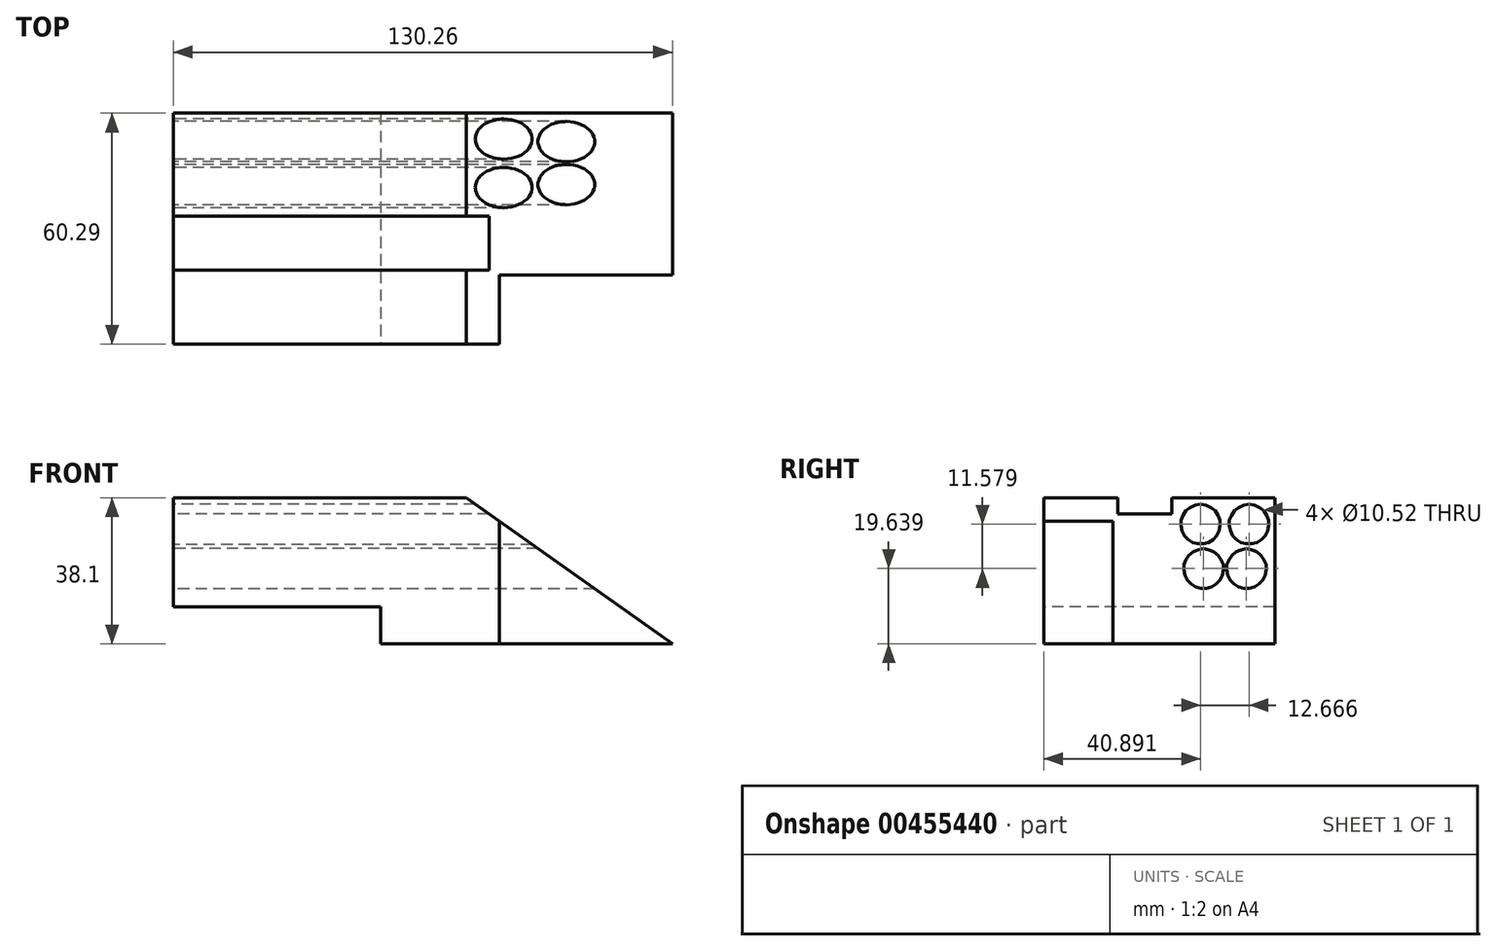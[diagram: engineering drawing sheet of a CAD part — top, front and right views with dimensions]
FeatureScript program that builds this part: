
annotation { "Feature Type Name" : "Feature", "Feature Type Description" : "" }
export const myFeature = defineFeature(function(context is Context, id is Id, definition is map)
    precondition{}
    {
        {
            var Q0;
            Q0=qCreatedBy(makeId("Top.planeOp"),FACE);
            var sketch = newSketch(context, id + "F0", { "sketchPlane" : qUnion([Q0])});
            skLineSegment(sketch, "E0.bottom", {"start": v(-48.16, 21.61) * mm, "end": v(82.1, 21.61) * mm});
            skLineSegment(sketch, "E0.top", {"start": v(-48.16, -38.68) * mm, "end": v(82.1, -38.68) * mm});
            skLineSegment(sketch, "E0.left", {"start": v(-48.16, 21.61) * mm, "end": v(-48.16, -38.68) * mm});
            skLineSegment(sketch, "E0.right", {"start": v(82.1, 21.61) * mm, "end": v(82.1, -38.68) * mm});
            skLineSegment(sketch, "E1.bottom", {"start": v(82.1, -38.68) * mm, "end": v(36.97, -38.68) * mm});
            skLineSegment(sketch, "E1.top", {"start": v(82.1, -20.67) * mm, "end": v(36.97, -20.67) * mm});
            skLineSegment(sketch, "E1.left", {"start": v(82.1, -38.68) * mm, "end": v(82.1, -20.67) * mm});
            skLineSegment(sketch, "E1.right", {"start": v(36.97, -38.68) * mm, "end": v(36.97, -20.67) * mm});
            skSolve(sketch);
        }
        {
            var Q0;
            Q0=makeQuery(id+"F0.imprint","IMPRINT",FACE,{"disambiguationData":[TD([[makeQuery(id+"F0.imprint","IMPRINT",EDGE,{"derivedFrom":sQuery(id+"F0.wireOp",EDGE,"E0.bottom")}),-1.0]])]});
            extrude(context, id + "F1", {"entities" : qUnion([Q0]), "depth" : 38.1 * mm});
        }
        {
            var Q0;
            Q0=makeQuery(id+"F1.opExtrude","SWEPT_FACE",FACE,{"disambiguationData":[OSD([sQuery(id+"F0.wireOp",EDGE,"E0.top")])]});
            var sketch = newSketch(context, id + "F2", { "sketchPlane" : qUnion([Q0])});
            skLineSegment(sketch, "E2", {"start": v(28.35, 38.1) * mm, "end": v(82.16, 0) * mm});
            skLineSegment(sketch, "E3", {"start": v(28.35, 38.1) * mm, "end": v(82.16, 38.1) * mm});
            skLineSegment(sketch, "E4", {"start": v(82.16, 38.1) * mm, "end": v(82.16, 0) * mm});
            skSolve(sketch);
        }
        {
            var Q0;
            Q0 = qSketchRegion(id + "F2", true);
            extrude(context, id + "F3", {"entities" : qUnion([Q0]), "operationType" : NewBodyOperationType.REMOVE, "endBound" : BoundingType.THROUGH_ALL, "oppositeDirection" : true, "depth" : 25.4 * mm});
        }
        {
            var Q0;
            Q0=makeQuery(id+"F1.opExtrude","SWEPT_FACE",FACE,{"disambiguationData":[OSD([sQuery(id+"F0.wireOp",EDGE,"E0.top")])]});
            var sketch = newSketch(context, id + "F4", { "sketchPlane" : qUnion([Q0])});
            skLineSegment(sketch, "E5.bottom", {"start": v(-48.16, 0) * mm, "end": v(5.98, 0) * mm});
            skLineSegment(sketch, "E5.top", {"start": v(-48.16, 9.67) * mm, "end": v(5.98, 9.67) * mm});
            skLineSegment(sketch, "E5.left", {"start": v(-48.16, 0) * mm, "end": v(-48.16, 9.67) * mm});
            skLineSegment(sketch, "E5.right", {"start": v(5.98, 0) * mm, "end": v(5.98, 9.67) * mm});
            skSolve(sketch);
        }
        {
            var Q0;
            Q0=makeQuery(id+"F1.opExtrude","SWEPT_FACE",FACE,{"disambiguationData":[OSD([sQuery(id+"F0.wireOp",EDGE,"E0.left")])]});
            var sketch = newSketch(context, id + "F5", { "sketchPlane" : qUnion([Q0])});
            skCircle(sketch, "E6", {"center": v(-14.88, 31.22) * mm, "radius": 5.26 * mm});
            skCircle(sketch, "E7", {"center": v(-2.21, 31.22) * mm, "radius": 5.26 * mm});
            skCircle(sketch, "E8", {"center": v(-14.2, 19.64) * mm, "radius": 5.26 * mm});
            skCircle(sketch, "E9", {"center": v(-3, 19.64) * mm, "radius": 5.26 * mm});
            skLineSegment(sketch, "E10.bottom", {"start": v(5.3, 38.1) * mm, "end": v(19.34, 38.1) * mm});
            skLineSegment(sketch, "E10.top", {"start": v(5.3, 33.94) * mm, "end": v(19.34, 33.94) * mm});
            skLineSegment(sketch, "E10.left", {"start": v(5.3, 38.1) * mm, "end": v(5.3, 33.94) * mm});
            skLineSegment(sketch, "E10.right", {"start": v(19.34, 38.1) * mm, "end": v(19.34, 33.94) * mm});
            skSolve(sketch);
        }
        {
            var Q0;
            Q0=makeQuery(id+"F5.imprint","IMPRINT",FACE,{"disambiguationData":[TD([[makeQuery(id+"F5.imprint","IMPRINT",EDGE,{"derivedFrom":sQuery(id+"F5.wireOp",EDGE,"E6")}),1.0]])]});
            var Q1;
            Q1=makeQuery(id+"F5.imprint","IMPRINT",FACE,{"disambiguationData":[TD([[makeQuery(id+"F5.imprint","IMPRINT",EDGE,{"derivedFrom":sQuery(id+"F5.wireOp",EDGE,"E7")}),1.0]])]});
            var Q2;
            Q2=makeQuery(id+"F5.imprint","IMPRINT",FACE,{"disambiguationData":[TD([[makeQuery(id+"F5.imprint","IMPRINT",EDGE,{"derivedFrom":sQuery(id+"F5.wireOp",EDGE,"E9")}),1.0]])]});
            var Q3;
            Q3=makeQuery(id+"F5.imprint","IMPRINT",FACE,{"disambiguationData":[TD([[makeQuery(id+"F5.imprint","IMPRINT",EDGE,{"derivedFrom":sQuery(id+"F5.wireOp",EDGE,"E8")}),1.0]])]});
            var Q4;
            Q4=makeQuery(id+"F5.imprint","IMPRINT",FACE,{"disambiguationData":[TD([[makeQuery(id+"F5.imprint","IMPRINT",EDGE,{"derivedFrom":sQuery(id+"F5.wireOp",EDGE,"E10.bottom")}),-1.0]])]});
            extrude(context, id + "F6", {"entities" : qUnion([Q0, Q1, Q2, Q3, Q4]), "operationType" : NewBodyOperationType.REMOVE, "endBound" : BoundingType.THROUGH_ALL, "oppositeDirection" : true, "depth" : 25.4 * mm});
        }
        {
            var Q0;
            Q0=makeQuery(id+"F4.imprint","IMPRINT",FACE,{"disambiguationData":[TD([[makeQuery(id+"F4.imprint","IMPRINT",EDGE,{"derivedFrom":sQuery(id+"F4.wireOp",EDGE,"E5.bottom")}),1.0]])]});
            extrude(context, id + "F7", {"entities" : qUnion([Q0]), "operationType" : NewBodyOperationType.REMOVE, "endBound" : BoundingType.THROUGH_ALL, "oppositeDirection" : true, "depth" : 25.4 * mm});
        }
    });
